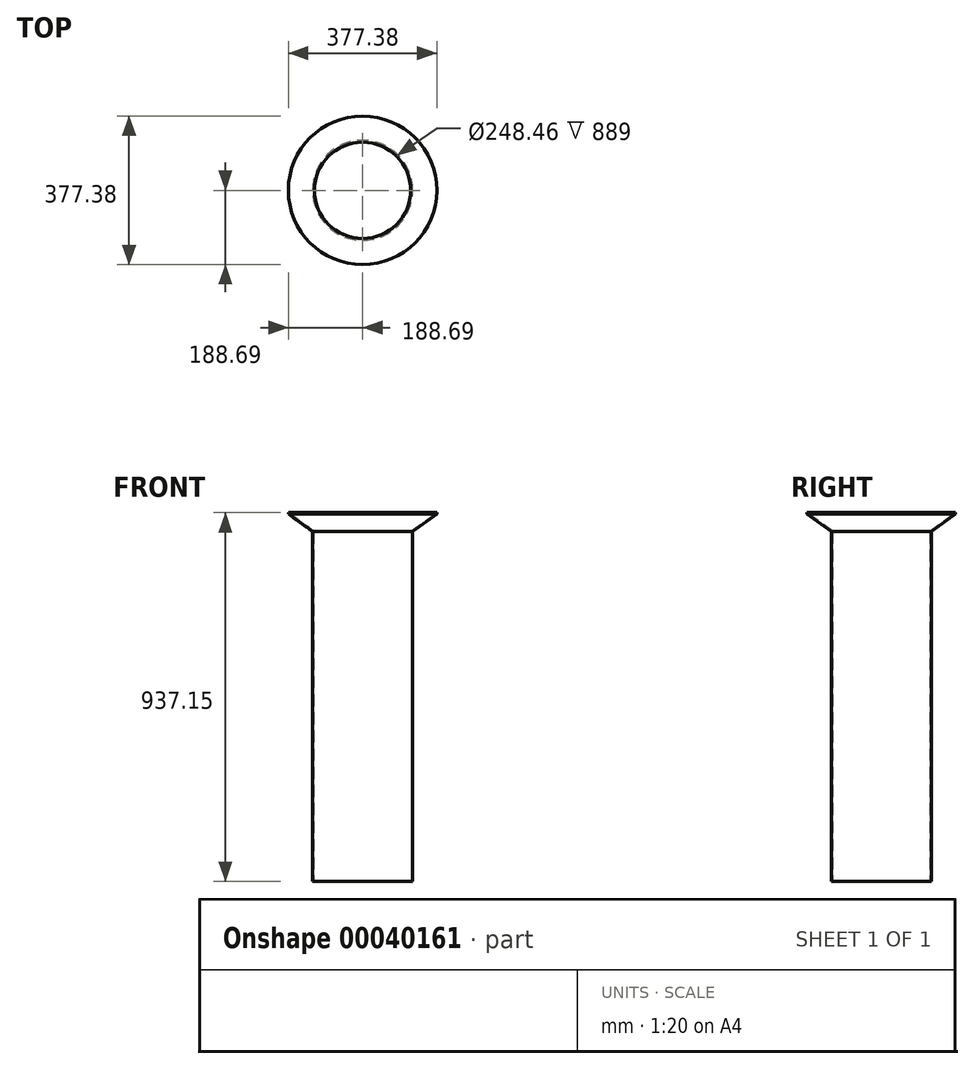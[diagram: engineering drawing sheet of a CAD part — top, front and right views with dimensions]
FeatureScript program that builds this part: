
annotation { "Feature Type Name" : "Feature", "Feature Type Description" : "" }
export const myFeature = defineFeature(function(context is Context, id is Id, definition is map)
    precondition{}
    {
        {
            var Q0;
            Q0=qCreatedBy(makeId("Top.planeOp"),FACE);
            var sketch = newSketch(context, id + "F0", { "sketchPlane" : qUnion([Q0])});
            skCircle(sketch, "E0", {"center": v(0, 0) * mm, "radius": 127 * mm});
            skCircle(sketch, "E1", {"center": v(0, 0) * mm, "radius": 124.23 * mm});
            skSolve(sketch);
        }
        {
            var Q0;
            Q0 = qSketchRegion(id + "F0", true);
            extrude(context, id + "F1", {"entities" : qUnion([Q0]), "depth" : 889 * mm});
        }
        {
            var Q0;
            Q0=qCreatedBy(makeId("Front.planeOp"),FACE);
            var sketch = newSketch(context, id + "F2", { "sketchPlane" : qUnion([Q0])});
            skLineSegment(sketch, "E2.0", {"start": v(-127, 889) * mm, "end": v(-122.28, 889) * mm});
            skLineSegment(sketch, "E3", {"start": v(-127, 889) * mm, "end": v(-188.7, 933.73) * mm});
            skLineSegment(sketch, "E4.0", {"start": v(-122.28, 889) * mm, "end": v(-188.7, 937.15) * mm});
            skLineSegment(sketch, "E5", {"start": v(-188.7, 933.73) * mm, "end": v(-188.7, 937.15) * mm});
            skPoint(sketch, "E6.orphan", {"position": v(127, 889) * mm});
            skLineSegment(sketch, "E7", {"start": v(0, 891.04) * mm, "end": v(0, 934.9) * mm});
            skSolve(sketch);
        }
        {
            var Q0;
            Q0=makeQuery(id+"F2.imprint","IMPRINT",FACE,{"disambiguationData":[TD([[makeQuery(id+"F2.imprint","IMPRINT",EDGE,{"derivedFrom":sQuery(id+"F2.wireOp",EDGE,"E3")}),-1.0]])]});
            var Q1;
            Q1=sQuery(id+"F2.wireOp",EDGE,"E7");
            revolve(context, id + "F3", {"entities" : qUnion([Q0]), "axis" : qUnion([Q1]), "revolveType" : RevolveType.FULL});
        }
    });
